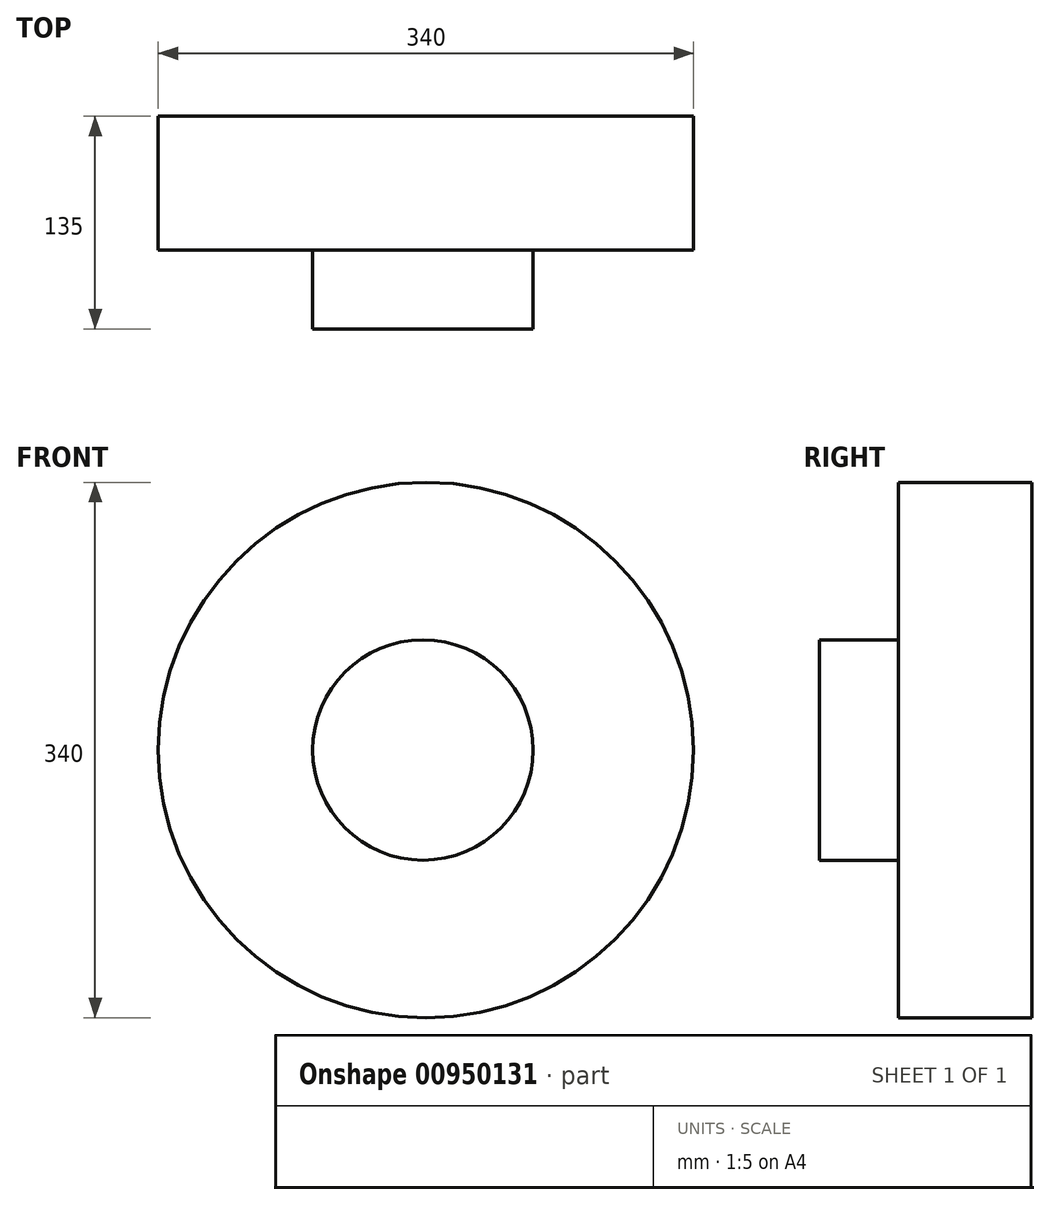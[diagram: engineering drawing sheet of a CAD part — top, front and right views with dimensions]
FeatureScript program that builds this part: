
annotation { "Feature Type Name" : "Feature", "Feature Type Description" : "" }
export const myFeature = defineFeature(function(context is Context, id is Id, definition is map)
    precondition{}
    {
        {
            var Q0;
            Q0=qCreatedBy(makeId("Front.planeOp"),FACE);
            var sketch = newSketch(context, id + "F0", { "sketchPlane" : qUnion([Q0])});
            skCircle(sketch, "E0", {"center": v(0, 0) * mm, "radius": 170 * mm});
            skSolve(sketch);
        }
        {
            var Q0;
            Q0=makeQuery(id+"F0.imprint","IMPRINT",FACE,{"disambiguationData":[TD([[makeQuery(id+"F0.imprint","IMPRINT",EDGE,{"derivedFrom":sQuery(id+"F0.wireOp",EDGE,"E0")}),1.0]])]});
            extrude(context, id + "F1", {"entities" : qUnion([Q0]), "depth" : 85 * mm, "offsetDistance" : 25 * mm});
        }
        {
            var Q0;
            Q0=makeQuery(id+"F1.opExtrude","CAP_FACE",FACE,{"disambiguationData":[OSD([sQuery(id+"F0.wireOp",EDGE,"E0")])],"isStart":false});
            var sketch = newSketch(context, id + "F2", { "sketchPlane" : qUnion([Q0])});
            skCircle(sketch, "E1", {"center": v(-1.9, 0) * mm, "radius": 70 * mm});
            skSolve(sketch);
        }
        {
            var Q0;
            Q0 = qSketchRegion(id + "F2", true);
            extrude(context, id + "F3", {"entities" : qUnion([Q0]), "operationType" : NewBodyOperationType.ADD, "depth" : 50 * mm, "offsetDistance" : 25 * mm});
        }
        {
            var Q0;
            Q0=makeQuery(id+"F3.opExtrude","CAP_FACE",FACE,{"disambiguationData":[OSD([sQuery(id+"F2.wireOp",EDGE,"E1")])],"isStart":false});
            var sketch = newSketch(context, id + "F4", { "sketchPlane" : qUnion([Q0])});
            skCircle(sketch, "E2", {"center": v(0, 0) * mm, "radius": 50 * mm});
            skSolve(sketch);
        }
        {
            var Q0;
            Q0 = qSketchRegion(id + "F4", true);
            var Q1;
            Q1=sQuery(id+"F4.wireOp",EDGE,"E2");
            extrude(context, id + "F5", {"entities" : qUnion([Q0]), "bodyType" : ToolBodyType.SURFACE, "surfaceEntities" : qUnion([Q1]), "depth" : 50 * mm, "offsetDistance" : 25 * mm});
        }
    });
